# Revit family: Bateria_czasowa_umywalkowa_stojaca_9090
name_source: partatom
category: Osprzęt hydrauliczny
units: mm (PartAtom-declared; Revit-internal decimal feet)

## family parameters
Obiekt nadrzędny = Powierzchnia
Punkt obliczania pomieszczeń = Nie
Tnij formami wycięć po wczytaniu = Nie
Typ części = Normalny
Współdzielony = Nie
Wymiar okrągłego złącza = Użyj średnicy

## types (1)
- FAN9090
    Depth / Glebokosc = 91 mm  [stored 0.298556 ft]
    Domyślna rzędna = 1219 mm
    Height / Wysokosc = 150 mm
    Komentarze do typu = Bateria czasowa umywalkowa stojąca 9090
    Manufacturer code / Kod producenta = 5901764296898
    Material = Mosiadz chromowany
    Material finish / Wykonczenie = Mosiądz pokryty chromem
    Opis = Cechy:
- Wysoka odporność na akty wandalizmu dzięki wykonaniu z najwyższej jakości materiałów
- Prosta obsługa
W zestawie:
- Wylewka wyposażona w standardowe sitko
- Bateria
- Zestaw montażowy do umywalki

Cechy:
- Wysoka odporność na akty wandalizmu dzięki wykonaniu z najwyższej jakości materiałów
- Prosta obsługa
- Łatwy montaż
    Producent = faneco.com
    Product code / Kod produktu = FAN9090
    URL = https://faneco.com
    Weight / Waga = 0.76 kg
    Width / Szerokosc = 46 mm  [stored 0.150919 ft]

note: [stored X ft] marks values corroborated as IEEE doubles in the binary element streams (Revit-internal decimal feet)

## geometry (parser evidence)
native form markers: Sweep x12
no freeform markers — native parametric forms only
